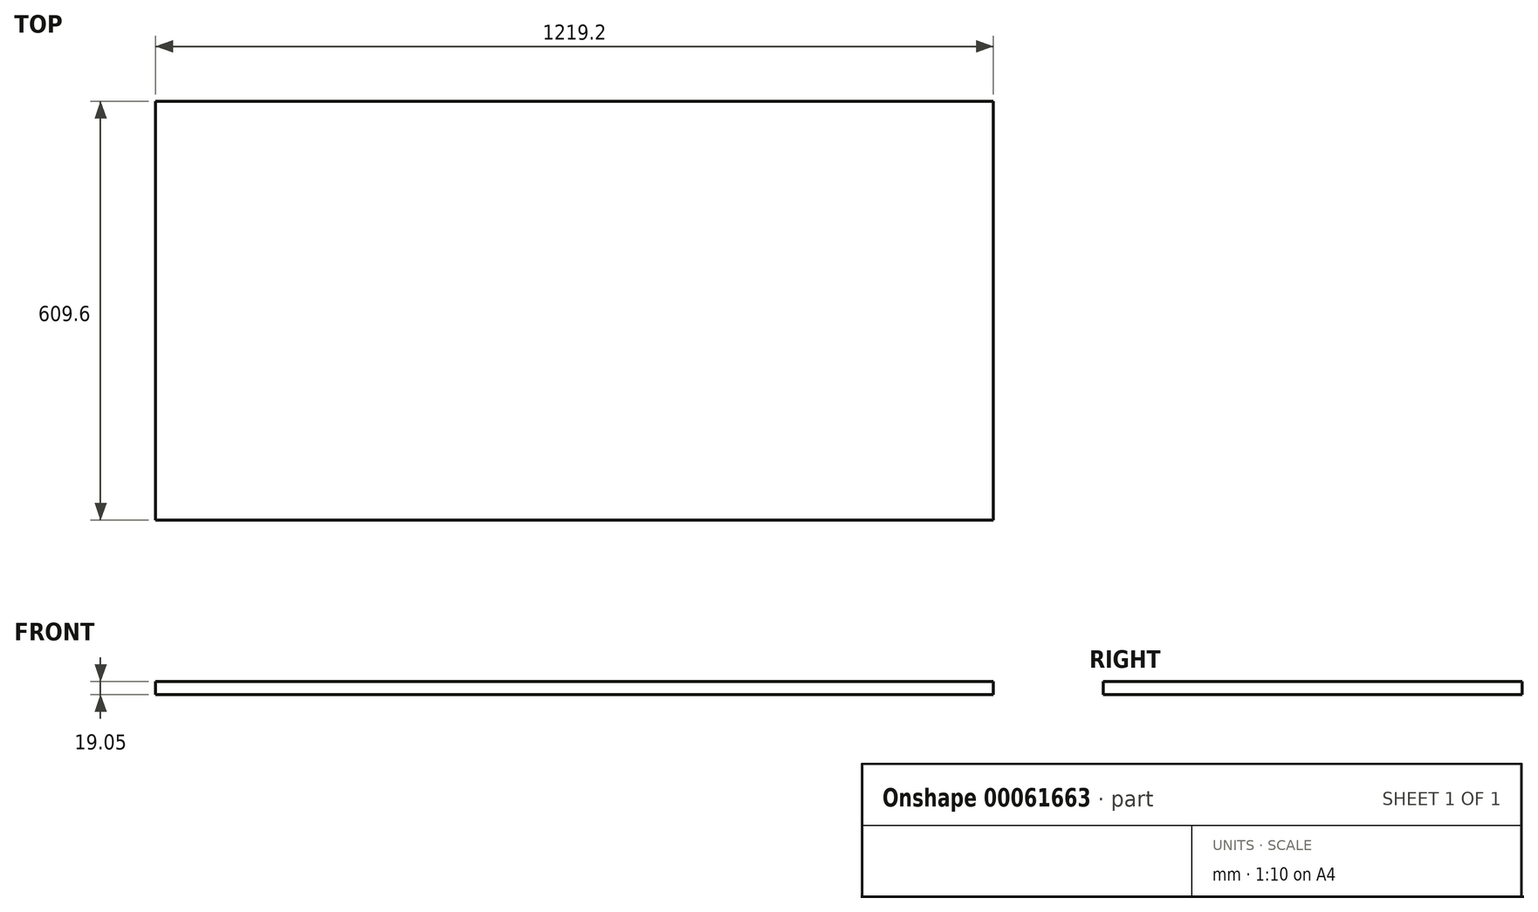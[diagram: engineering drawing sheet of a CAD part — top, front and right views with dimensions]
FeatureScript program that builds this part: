
annotation { "Feature Type Name" : "Feature", "Feature Type Description" : "" }
export const myFeature = defineFeature(function(context is Context, id is Id, definition is map)
    precondition{}
    {
        {
            var Q0;
            Q0=qCreatedBy(makeId("Top.planeOp"),FACE);
            var sketch = newSketch(context, id + "F0", { "sketchPlane" : qUnion([Q0])});
            skLineSegment(sketch, "E0.bottom", {"start": v(0, 0) * mm, "end": v(1219.2, 0) * mm});
            skLineSegment(sketch, "E0.top", {"start": v(0, 609.6) * mm, "end": v(1219.2, 609.6) * mm});
            skLineSegment(sketch, "E0.left", {"start": v(0, 0) * mm, "end": v(0, 609.6) * mm});
            skLineSegment(sketch, "E0.right", {"start": v(1219.2, 0) * mm, "end": v(1219.2, 609.6) * mm});
            skSolve(sketch);
        }
        {
            var Q0;
            Q0 = qSketchRegion(id + "F0", true);
            extrude(context, id + "F1", {"entities" : qUnion([Q0]), "depth" : 19.05 * mm});
        }
    });
